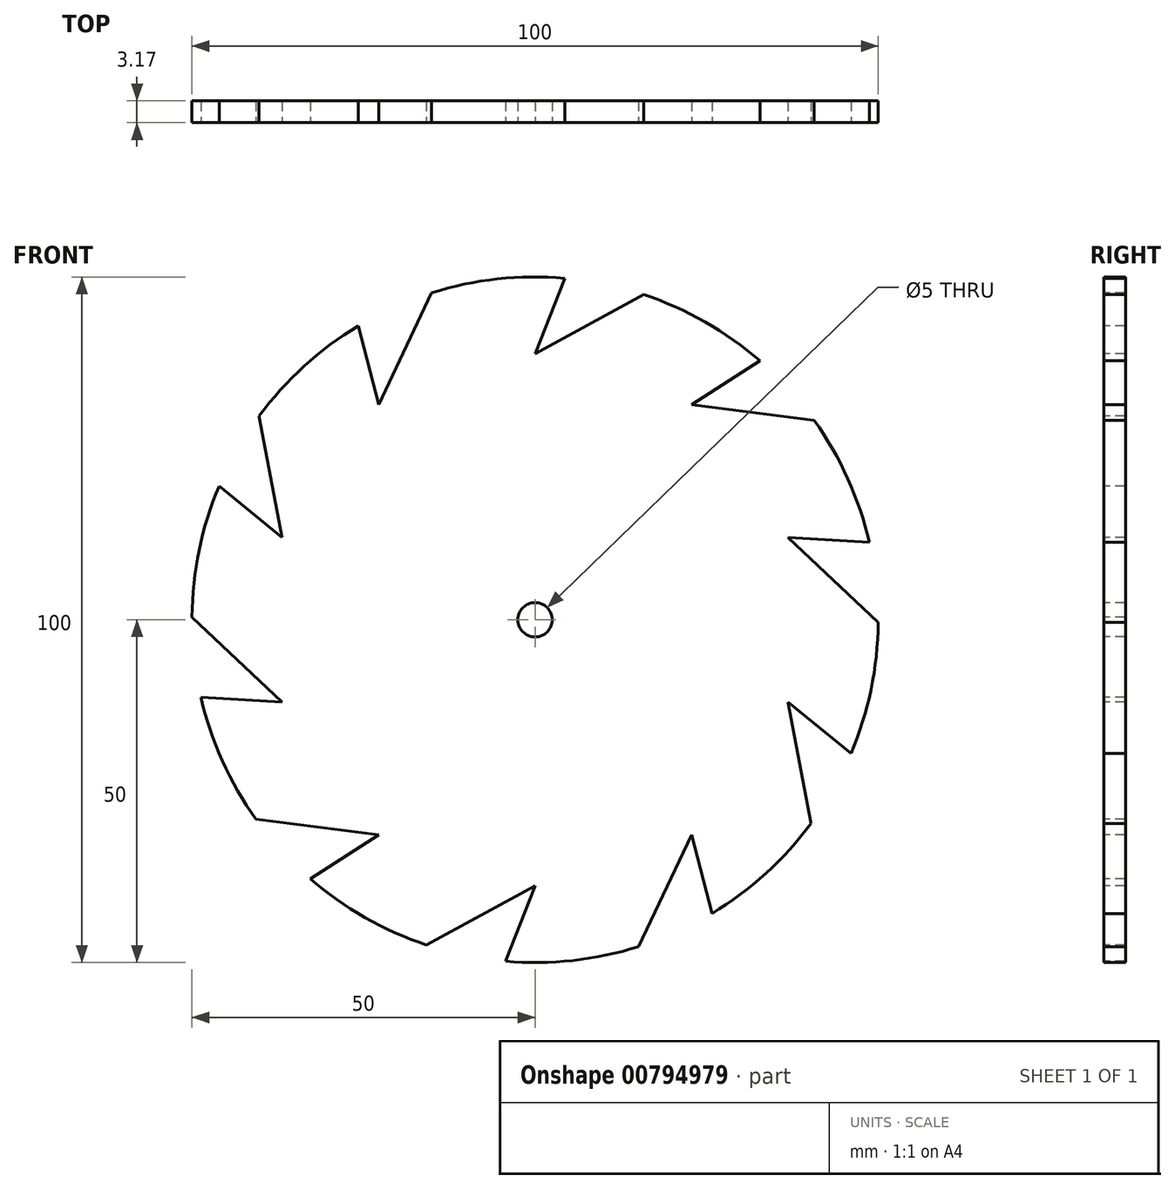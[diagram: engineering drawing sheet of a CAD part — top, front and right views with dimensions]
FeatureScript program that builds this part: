
annotation { "Feature Type Name" : "Feature", "Feature Type Description" : "" }
export const myFeature = defineFeature(function(context is Context, id is Id, definition is map)
    precondition{}
    {
        {
            var Q0;
            Q0=qCreatedBy(makeId("Front.planeOp"),FACE);
            var sketch = newSketch(context, id + "F0", { "sketchPlane" : qUnion([Q0])});
            skCircle(sketch, "E0", {"center": v(0, 0) * mm, "radius": 50 * mm});
            skSolve(sketch);
        }
        {
            var Q0;
            Q0=makeQuery(id+"F0.imprint","IMPRINT",FACE,{"disambiguationData":[TD([[makeQuery(id+"F0.imprint","IMPRINT",EDGE,{"derivedFrom":sQuery(id+"F0.wireOp",EDGE,"E0")}),1.0]])]});
            extrude(context, id + "F1", {"entities" : qUnion([Q0]), "depth" : 3.17 * mm, "offsetDistance" : 25 * mm});
        }
        {
            var Q0;
            Q0=makeQuery(id+"F1.opExtrude","CAP_FACE",FACE,{"disambiguationData":[OSD([sQuery(id+"F0.wireOp",EDGE,"E0")])],"isStart":false});
            var sketch = newSketch(context, id + "F2", { "sketchPlane" : qUnion([Q0])});
            skCircle(sketch, "E1", {"center": v(0, 0) * mm, "radius": 2.5 * mm});
            skSolve(sketch);
        }
        {
            var Q0;
            Q0=makeQuery(id+"F2.imprint","IMPRINT",FACE,{"disambiguationData":[TD([[makeQuery(id+"F2.imprint","IMPRINT",EDGE,{"derivedFrom":sQuery(id+"F2.wireOp",EDGE,"E1")}),1.0]])]});
            extrude(context, id + "F3", {"entities" : qUnion([Q0]), "operationType" : NewBodyOperationType.REMOVE, "oppositeDirection" : true, "depth" : 25 * mm, "offsetDistance" : 25 * mm});
        }
        {
            var Q0;
            Q0=makeQuery(id+"F1.opExtrude","CAP_FACE",FACE,{"disambiguationData":[OSD([sQuery(id+"F0.wireOp",EDGE,"E0")])],"isStart":false});
            var sketch = newSketch(context, id + "F4", { "sketchPlane" : qUnion([Q0])});
            skLineSegment(sketch, "E2", {"start": v(15.84, 47.43) * mm, "end": v(0, 38.78) * mm});
            skLineSegment(sketch, "E3", {"start": v(0, 38.78) * mm, "end": v(4.31, 49.81) * mm});
            skLineSegment(sketch, "E4.1.0", {"start": v(-15.06, 47.68) * mm, "end": v(-22.8, 31.37) * mm});
            skLineSegment(sketch, "E4.1.1", {"start": v(-22.8, 31.37) * mm, "end": v(-25.79, 42.84) * mm});
            skLineSegment(sketch, "E4.2.0", {"start": v(-40.2, 29.72) * mm, "end": v(-36.88, 11.98) * mm});
            skLineSegment(sketch, "E4.2.1", {"start": v(-36.88, 11.98) * mm, "end": v(-46.04, 19.5) * mm});
            skLineSegment(sketch, "E4.3.0", {"start": v(-50, 0.4) * mm, "end": v(-36.88, -11.98) * mm});
            skLineSegment(sketch, "E4.3.1", {"start": v(-36.88, -11.98) * mm, "end": v(-48.7, -11.29) * mm});
            skLineSegment(sketch, "E4.4.0", {"start": v(-40.69, -29.06) * mm, "end": v(-22.8, -31.37) * mm});
            skLineSegment(sketch, "E4.4.1", {"start": v(-22.8, -31.37) * mm, "end": v(-32.77, -37.76) * mm});
            skLineSegment(sketch, "E4.5.0", {"start": v(-15.84, -47.43) * mm, "end": v(0, -38.78) * mm});
            skLineSegment(sketch, "E4.5.1", {"start": v(0, -38.78) * mm, "end": v(-4.31, -49.81) * mm});
            skLineSegment(sketch, "E4.6.0", {"start": v(15.06, -47.68) * mm, "end": v(22.8, -31.37) * mm});
            skLineSegment(sketch, "E4.6.1", {"start": v(22.8, -31.37) * mm, "end": v(25.79, -42.84) * mm});
            skLineSegment(sketch, "E4.7.0", {"start": v(40.2, -29.72) * mm, "end": v(36.88, -11.98) * mm});
            skLineSegment(sketch, "E4.7.1", {"start": v(36.88, -11.98) * mm, "end": v(46.04, -19.5) * mm});
            skLineSegment(sketch, "E4.8.0", {"start": v(50, -0.4) * mm, "end": v(36.88, 11.98) * mm});
            skLineSegment(sketch, "E4.8.1", {"start": v(36.88, 11.98) * mm, "end": v(48.7, 11.29) * mm});
            skLineSegment(sketch, "E4.9.0", {"start": v(40.69, 29.06) * mm, "end": v(22.8, 31.37) * mm});
            skLineSegment(sketch, "E4.9.1", {"start": v(22.8, 31.37) * mm, "end": v(32.77, 37.76) * mm});
            skPoint(sketch, "E4.center", {"position": v(0, 0) * mm});
            skSolve(sketch);
        }
        {
            var Q0;
            {var subQ0=sQuery(id+"F4.wireOp",EDGE,"E4.1.0");Q0=makeQuery(id+"F4.imprint","IMPRINT",FACE,{"disambiguationData":[TD([[makeQuery(id+"F4.imprint","IMPRINT",EDGE,{"derivedFrom":subQ0}),-1.0]])]});}
            var Q1;
            {var subQ0=sQuery(id+"F4.wireOp",EDGE,"E2");Q1=makeQuery(id+"F4.imprint","IMPRINT",FACE,{"disambiguationData":[TD([[makeQuery(id+"F4.imprint","IMPRINT",EDGE,{"derivedFrom":subQ0}),-1.0]])]});}
            var Q2;
            {var subQ0=sQuery(id+"F4.wireOp",EDGE,"E4.9.0");Q2=makeQuery(id+"F4.imprint","IMPRINT",FACE,{"disambiguationData":[TD([[makeQuery(id+"F4.imprint","IMPRINT",EDGE,{"derivedFrom":subQ0}),-1.0]])]});}
            var Q3;
            {var subQ0=sQuery(id+"F4.wireOp",EDGE,"E4.8.0");Q3=makeQuery(id+"F4.imprint","IMPRINT",FACE,{"disambiguationData":[TD([[makeQuery(id+"F4.imprint","IMPRINT",EDGE,{"derivedFrom":subQ0}),-1.0]])]});}
            var Q4;
            {var subQ0=sQuery(id+"F4.wireOp",EDGE,"E4.7.0");Q4=makeQuery(id+"F4.imprint","IMPRINT",FACE,{"disambiguationData":[TD([[makeQuery(id+"F4.imprint","IMPRINT",EDGE,{"derivedFrom":subQ0}),-1.0]])]});}
            var Q5;
            {var subQ0=sQuery(id+"F4.wireOp",EDGE,"E4.6.0");Q5=makeQuery(id+"F4.imprint","IMPRINT",FACE,{"disambiguationData":[TD([[makeQuery(id+"F4.imprint","IMPRINT",EDGE,{"derivedFrom":subQ0}),-1.0]])]});}
            var Q6;
            {var subQ0=sQuery(id+"F4.wireOp",EDGE,"E4.5.0");Q6=makeQuery(id+"F4.imprint","IMPRINT",FACE,{"disambiguationData":[TD([[makeQuery(id+"F4.imprint","IMPRINT",EDGE,{"derivedFrom":subQ0}),-1.0]])]});}
            var Q7;
            {var subQ0=sQuery(id+"F4.wireOp",EDGE,"E4.4.0");Q7=makeQuery(id+"F4.imprint","IMPRINT",FACE,{"disambiguationData":[TD([[makeQuery(id+"F4.imprint","IMPRINT",EDGE,{"derivedFrom":subQ0}),-1.0]])]});}
            var Q8;
            {var subQ0=sQuery(id+"F4.wireOp",EDGE,"E4.3.0");Q8=makeQuery(id+"F4.imprint","IMPRINT",FACE,{"disambiguationData":[TD([[makeQuery(id+"F4.imprint","IMPRINT",EDGE,{"derivedFrom":subQ0}),-1.0]])]});}
            var Q9;
            {var subQ0=sQuery(id+"F4.wireOp",EDGE,"E4.2.0");Q9=makeQuery(id+"F4.imprint","IMPRINT",FACE,{"disambiguationData":[TD([[makeQuery(id+"F4.imprint","IMPRINT",EDGE,{"derivedFrom":subQ0}),-1.0]])]});}
            extrude(context, id + "F5", {"entities" : qUnion([Q0, Q1, Q2, Q3, Q4, Q5, Q6, Q7, Q8, Q9]), "operationType" : NewBodyOperationType.REMOVE, "oppositeDirection" : true, "depth" : 25 * mm, "offsetDistance" : 25 * mm});
        }
    });
